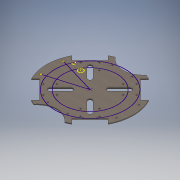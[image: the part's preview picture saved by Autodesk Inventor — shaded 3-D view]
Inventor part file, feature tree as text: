
AUTODESK INVENTOR PART (.ipt)
format: ipt  version: 2020 (Build 240168000, 168)  size: 457,728 bytes
history: native  units: mm
features: sketch x7, extrude x5, projected_geometry x2, other x1
ambient origin geometry x8: Origin, YZ Plane, XZ Plane, XY Plane, X Axis, Y Axis, Z Axis, Center Point
bodies: Body1 (feature_tree)
feature tree (15):
  other  "Твердое тело1"
  extrude  "Выдавливание1"  Depth=2.0mm TaperAngle=0.0deg
  sketch  "Эскиз3"
  extrude  "Выдавливание5"  Depth=6.342mm
  sketch  "Эскиз6"
  sketch  "Эскиз7"
  extrude  "Выдавливание4"  Depth=16.0mm
  sketch  "Эскиз8"
  extrude  "Выдавливание6"  Depth=3.0mm
  sketch  "Эскиз9"
  sketch  "Эскиз10"
  extrude  "Выдавливание7"  Depth=3.0mm
  sketch  "Эскиз12"
  projected_geometry  "Спроецированная петля1"
  projected_geometry  "Спроецированная петля2"
